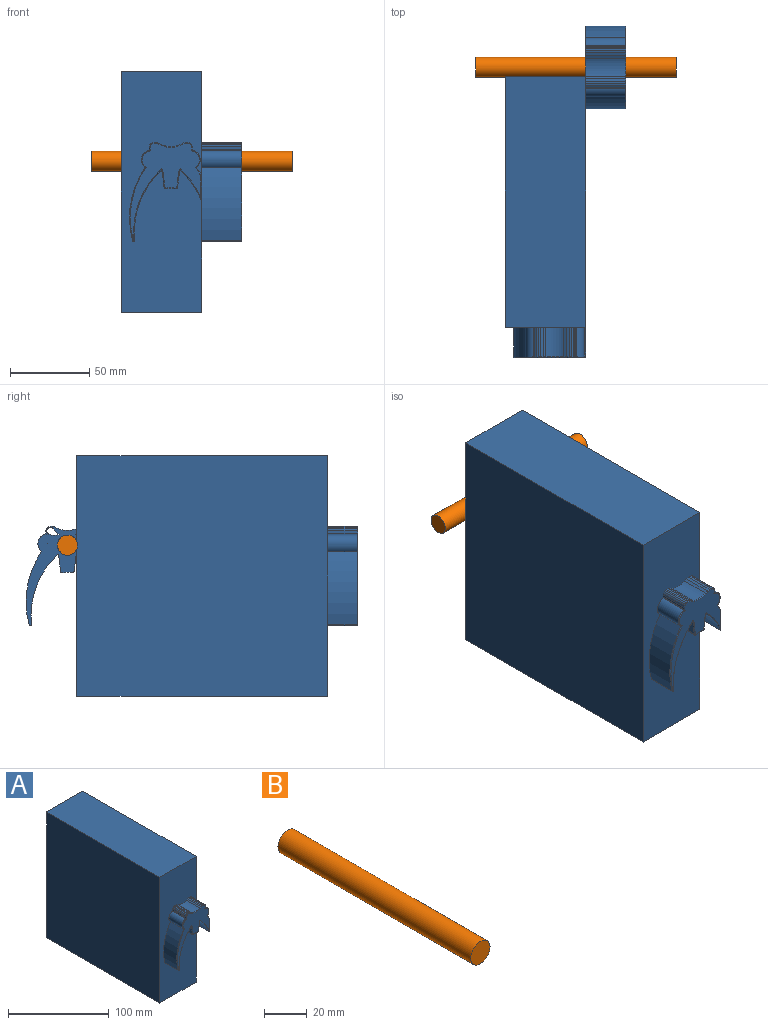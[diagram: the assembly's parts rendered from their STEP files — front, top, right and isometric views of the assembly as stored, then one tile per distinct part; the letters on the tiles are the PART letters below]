
ASSEMBLY  parts=2 mates=1
PART A: 129 faces, bbox 76.2x209.9x152.4 mm
  f0: plane 4.51x0.41mm, normal (1,0,0), area 1.3mm2, adj f6,f123
  f1: plane 7.02x5.02mm, normal (1,0,0), area 23.2mm2, adj f6,f82,f83,f122
  f2: plane 158.75x152.4mm, normal (-1,0,0), area 24193.5mm2, adj f3,f5,f6,f7
  f3: plane 158.75x50.8mm, normal (0,0,-1), area 8064.5mm2, adj f2,f4,f6,f7
  f4: plane 177.29x152.4mm, normal (1,0,0), area 24066.4mm2, adj f3,f5,f6,f7,f40,f41,f79,f87
  f5: plane 158.75x50.8mm, normal (0,0,1), area 8064.5mm2, adj f2,f4,f6,f7
  f6: plane 152.4x50.8mm, normal (0,1,0), area 7741.9mm2, adj f0,f1,f2,f3,f4,f5,f128
  f7: plane 152.4x50.8mm, normal (0,-1,0), area 6728.2mm2, adj f2,f3,f4,f5,f8,f9,f10,f11
  f8: plane 18.54x0.74mm, normal (-0.98,0,-0.2), area 14mm2, adj f7,f9,f27,f50
  f9: plane 18.54x1.46mm, normal (-1,0,0), area 27.1mm2, adj f7,f8,f10,f48
  f10: plane 18.54x1.2mm, normal (-0.96,0,0.27), area 23.2mm2, adj f7,f9,f11,f46
  f11: plane 18.54x0.9mm, normal (-0.81,0,0.59), area 20.6mm2, adj f7,f10,f12,f44
  f12: plane 18.54x0.95mm, normal (-0.51,0,0.86), area 20.5mm2, adj f7,f11,f13,f45
  f13: plane 18.54x1.21mm, normal (-0.17,0,0.99), area 22.8mm2, adj f7,f12,f14,f47
  f14: plane 18.54x1.43mm, normal (0.11,0,0.99), area 26.7mm2, adj f7,f13,f15,f49
  f15: plane 18.54x1.59mm, normal (0.31,0,0.95), area 31mm2, adj f7,f14,f26,f51
  f16: plane 18.54x1.69mm, normal (-0.45,0,0.89), area 35.2mm2, adj f7,f17,f25,f57
  f17: plane 18.54x1.59mm, normal (-0.31,0,0.95), area 31mm2, adj f7,f16,f18,f59
  f18: plane 18.54x1.43mm, normal (-0.11,0,0.99), area 26.7mm2, adj f7,f17,f19,f61
  f19: plane 18.54x1.21mm, normal (0.17,0,0.99), area 22.8mm2, adj f7,f18,f20,f63
  f20: plane 18.54x0.95mm, normal (0.51,0,0.86), area 20.5mm2, adj f7,f19,f21,f65
  f21: plane 18.54x0.9mm, normal (0.81,0,0.59), area 20.6mm2, adj f7,f20,f22,f67
  f22: plane 18.54x1.2mm, normal (0.96,0,0.27), area 23.2mm2, adj f7,f21,f23,f69
  f23: plane 18.54x1.46mm, normal (1,0,0), area 27.1mm2, adj f7,f22,f24,f71
  f24: plane 18.54x0.74mm, normal (0.98,0,-0.2), area 14mm2, adj f7,f23,f42,f73
  f25: cylinder r=14.29mm len=18.54mm, axis (0,1,0), area 217.9mm2, adj f7,f16,f26,f55
  f26: plane 18.54x1.69mm, normal (0.45,0,0.89), area 35.2mm2, adj f7,f15,f25,f53
  f27: cylinder r=6.29mm len=18.54mm, axis (0,1,0), area 265mm2, adj f7,f8,f28,f52
  f28: cylinder r=56.15mm len=46.32mm, axis (0,1,0), area 898.7mm2, adj f7,f27,f29,f54
  f29: cylinder r=0.67mm len=18.54mm, axis (0,1,0), area 18.2mm2, adj f7,f28,f30,f56
  f30: cylinder r=0.64mm len=18.54mm, axis (0,1,0), area 20.2mm2, adj f7,f29,f31,f58
  f31: cylinder r=53.73mm len=44.61mm, axis (0,1,0), area 915.5mm2, adj f7,f30,f32,f60
  f32: cylinder r=3.17mm len=18.54mm, axis (0,1,0), area 29.3mm2, adj f7,f31,f33,f62
  f33: plane 18.54x9.47mm, normal (-0.99,0,-0.12), area 176.9mm2, adj f7,f32,f34,f64
  f34: cylinder r=1.11mm len=18.54mm, axis (0,1,0), area 36.1mm2, adj f7,f33,f35,f66
  f35: cylinder r=10.43mm len=18.54mm, axis (0,1,0), area 53.3mm2, adj f7,f34,f36,f68
  f36: cylinder r=10.43mm len=18.54mm, axis (0,1,0), area 53.3mm2, adj f7,f35,f37,f70
  f37: cylinder r=1.11mm len=18.54mm, axis (0,1,0), area 36.1mm2, adj f7,f36,f38,f72
  f38: plane 18.54x9.47mm, normal (0.99,0,-0.12), area 176.9mm2, adj f7,f37,f39,f74
  f39: cylinder r=3.17mm len=18.54mm, axis (0,1,0), area 29.3mm2, adj f7,f38,f40,f76
  f40: cylinder r=53.72mm len=19.87mm, axis (0,1,0), area 448.4mm2, adj f4,f7,f39,f78
  f41: cylinder r=56.14mm len=18.54mm, axis (0,1,0), area 108.7mm2, adj f4,f7,f42,f77
  f42: cylinder r=6.29mm len=18.54mm, axis (0,1,0), area 265mm2, adj f7,f24,f41,f75
  f43: plane 61.88x44.54mm, normal (0,-1,0), area 892mm2, adj f44,f45,f46,f47,f48,f49,f50,f51
  f44: cylinder r=0.51mm len=1.2mm, axis (0.59,0,0.81), area 0.8mm2, adj f11,f43,f45,f46
  f45: cylinder r=0.51mm len=1.21mm, axis (0.86,0,0.51), area 0.8mm2, adj f12,f43,f44,f47
  f46: cylinder r=0.51mm len=1.34mm, axis (0.27,0,0.96), area 0.9mm2, adj f10,f43,f44,f48
  f47: cylinder r=0.51mm len=1.3mm, axis (0.99,0,0.17), area 0.9mm2, adj f13,f43,f45,f49
  f48: cylinder r=0.51mm len=1.46mm, axis (0,0,1), area 1.1mm2, adj f9,f43,f46,f50
  f49: cylinder r=0.51mm len=1.49mm, axis (0.99,0,-0.11), area 1.1mm2, adj f14,f43,f47,f51
  f50: cylinder r=0.51mm len=1.37mm, axis (-0.2,0,0.98), area 0.7mm2, adj f8,f43,f48,f52
  f51: cylinder r=0.51mm len=1.75mm, axis (0.95,0,-0.31), area 1.3mm2, adj f15,f43,f49,f53
  f52: torus R=5.78mm, axis (0,-1,0), area 11.4mm2, adj f27,f43,f50,f54
  f53: cylinder r=0.51mm len=1.94mm, axis (0.89,0,-0.45), area 1.5mm2, adj f26,f43,f51,f55
  f54: torus R=55.64mm, axis (0,-1,0), area 38.7mm2, adj f28,f43,f52,f56
  f55: torus R=14.8mm, axis (0,-1,0), area 9.5mm2, adj f25,f43,f53,f57
  f56: torus R=0.17mm, axis (0,-1,0), area 0.6mm2, adj f29,f43,f54,f58
  f57: cylinder r=0.51mm len=1.94mm, axis (0.89,0,0.45), area 1.5mm2, adj f16,f43,f55,f59
  f58: torus R=0.13mm, axis (0,-1,0), area 0.6mm2, adj f30,f43,f56,f60
  f59: cylinder r=0.51mm len=1.75mm, axis (0.95,0,0.31), area 1.3mm2, adj f17,f43,f57,f61
  f60: torus R=54.23mm, axis (0,-1,0), area 39.7mm2, adj f31,f43,f58,f62
  f61: cylinder r=0.51mm len=1.49mm, axis (0.99,0,0.11), area 1.1mm2, adj f18,f43,f59,f63
  f62: torus R=3.68mm, axis (0,-1,0), area 1.5mm2, adj f32,f43,f60,f64
  f63: cylinder r=0.51mm len=1.3mm, axis (0.99,0,-0.17), area 0.9mm2, adj f19,f43,f61,f65
  f64: cylinder r=0.51mm len=9.53mm, axis (-0.12,0,0.99), area 7.6mm2, adj f33,f43,f62,f66
  f65: cylinder r=0.51mm len=1.21mm, axis (0.86,0,-0.51), area 0.8mm2, adj f20,f43,f63,f67
  f66: torus R=0.6mm, axis (0,-1,0), area 1.3mm2, adj f34,f43,f64,f68
  f67: cylinder r=0.51mm len=1.2mm, axis (0.59,0,-0.81), area 0.8mm2, adj f21,f43,f65,f69
  f68: torus R=10.94mm, axis (0,-1,0), area 2.3mm2, adj f35,f43,f66,f70
  f69: cylinder r=0.51mm len=1.34mm, axis (0.27,0,-0.96), area 0.9mm2, adj f22,f43,f67,f71
  f70: torus R=10.94mm, axis (0,-1,0), area 2.3mm2, adj f36,f43,f68,f72
  f71: cylinder r=0.51mm len=1.46mm, axis (0,0,-1), area 1.1mm2, adj f23,f43,f69,f73
  f72: torus R=0.6mm, axis (0,-1,0), area 1.3mm2, adj f37,f43,f70,f74
  f73: cylinder r=0.51mm len=1.37mm, axis (-0.2,0,-0.98), area 0.7mm2, adj f24,f43,f71,f75
  f74: cylinder r=0.51mm len=9.53mm, axis (-0.12,0,-0.99), area 7.6mm2, adj f38,f43,f72,f76
  f75: torus R=5.78mm, axis (0,-1,0), area 11.4mm2, adj f42,f43,f73,f77
  f76: torus R=3.68mm, axis (0,-1,0), area 1.5mm2, adj f39,f43,f74,f78
  f77: torus R=55.64mm, axis (0,-1,0), area 4.7mm2, adj f41,f43,f75,f79
  f78: torus R=54.23mm, axis (0,-1,0), area 18.8mm2, adj f40,f43,f76,f79
  f79: cylinder r=0.51mm len=16.36mm, axis (0,0,-1), area 12.2mm2, adj f4,f43,f77,f78
  f80: cylinder r=8.13mm len=25.4mm, axis (-1,0,0), area 168.6mm2, adj f81,f126,f127,f128
  f81: cylinder r=10.32mm len=25.4mm, axis (-1,0,0), area 132.3mm2, adj f80,f126,f127,f128
  f82: cylinder r=10.32mm len=25.4mm, axis (-1,0,0), area 132.3mm2, adj f1,f83,f122,f127,f128
  f83: cylinder r=8.13mm len=25.4mm, axis (-1,0,0), area 168.6mm2, adj f1,f82,f122,f127,f128
  f84: plane 25.4x0mm, normal (0,-0.73,0.68), area 0mm2, adj f85,f124,f127,f128
  f85: cylinder r=56.14mm len=25.4mm, axis (-1,0,0), area 0mm2, adj f84,f124,f127,f128
  f86: cylinder r=14.29mm len=25.4mm, axis (-1,0,0), area 298.5mm2, adj f87,f125,f127,f128
  f87: plane 25.4x1.69mm, normal (0,0.45,0.89), area 48.3mm2, adj f4,f86,f88,f127,f128
  f88: plane 25.4x1.59mm, normal (0,0.31,0.95), area 42.5mm2, adj f4,f87,f89,f127
  f89: plane 25.4x1.43mm, normal (0,0.11,0.99), area 36.5mm2, adj f4,f88,f90,f127
  f90: plane 25.4x1.21mm, normal (0,-0.17,0.99), area 31.3mm2, adj f4,f89,f91,f127
  f91: plane 25.4x0.95mm, normal (0,-0.51,0.86), area 28.1mm2, adj f4,f90,f92,f127
  f92: plane 25.4x0.9mm, normal (0,-0.81,0.59), area 28.3mm2, adj f4,f91,f93,f127
  f93: plane 25.4x1.2mm, normal (0,-0.96,0.27), area 31.7mm2, adj f4,f92,f94,f127
  f94: plane 25.4x1.46mm, normal (0,-1,0), area 37.1mm2, adj f4,f93,f95,f127
  f95: plane 25.4x0.74mm, normal (0,-0.98,-0.2), area 19.2mm2, adj f4,f94,f96,f127
  f96: cylinder r=6.29mm len=25.4mm, axis (-1,0,0), area 363mm2, adj f4,f95,f97,f127
  f97: cylinder r=56.15mm len=46.32mm, axis (-1,0,0), area 1231.1mm2, adj f4,f96,f98,f127
  f98: cylinder r=0.67mm len=25.4mm, axis (-1,0,0), area 24.9mm2, adj f4,f97,f99,f127
  f99: cylinder r=0.64mm len=25.4mm, axis (-1,0,0), area 27.7mm2, adj f4,f98,f100,f127
  f100: cylinder r=53.73mm len=44.61mm, axis (-1,0,0), area 1254.2mm2, adj f4,f99,f101,f127
  f101: cylinder r=3.17mm len=25.4mm, axis (-1,0,0), area 40.2mm2, adj f4,f100,f102,f127,f128
  f102: plane 25.4x9.47mm, normal (0,-0.99,-0.12), area 242.3mm2, adj f101,f103,f127,f128
  f103: cylinder r=1.11mm len=25.4mm, axis (-1,0,0), area 49.4mm2, adj f102,f104,f127,f128
  f104: cylinder r=10.43mm len=25.4mm, axis (-1,0,0), area 73.1mm2, adj f103,f105,f127,f128
  f105: cylinder r=10.43mm len=25.4mm, axis (-1,0,0), area 73.1mm2, adj f104,f106,f127,f128
  f106: cylinder r=1.11mm len=25.4mm, axis (-1,0,0), area 49.4mm2, adj f105,f107,f127,f128
  f107: plane 25.4x9.47mm, normal (0,0.99,-0.12), area 242.3mm2, adj f106,f108,f127,f128
  f108: cylinder r=3.17mm len=25.4mm, axis (-1,0,0), area 40.2mm2, adj f107,f109,f127,f128
  f109: cylinder r=53.72mm len=44.61mm, axis (-1,0,0), area 1254.1mm2, adj f108,f110,f127,f128
  f110: cylinder r=0.64mm len=25.4mm, axis (-1,0,0), area 27.7mm2, adj f109,f111,f127,f128
  f111: cylinder r=0.67mm len=25.4mm, axis (-1,0,0), area 24.9mm2, adj f110,f112,f127,f128
  f112: cylinder r=56.14mm len=46.32mm, axis (-1,0,0), area 1231mm2, adj f111,f113,f127,f128
  f113: cylinder r=6.29mm len=25.4mm, axis (-1,0,0), area 363mm2, adj f112,f114,f127,f128
  f114: plane 25.4x0.74mm, normal (0,0.98,-0.2), area 19.2mm2, adj f113,f115,f127,f128
  f115: plane 25.4x1.46mm, normal (0,1,0), area 37.1mm2, adj f114,f116,f127,f128
  f116: plane 25.4x1.2mm, normal (0,0.96,0.27), area 31.7mm2, adj f115,f117,f127,f128
  f117: plane 25.4x0.9mm, normal (0,0.81,0.59), area 28.3mm2, adj f116,f118,f127,f128
  f118: plane 25.4x0.95mm, normal (0,0.51,0.86), area 28.1mm2, adj f117,f119,f127,f128
  f119: plane 25.4x1.21mm, normal (0,0.17,0.99), area 31.3mm2, adj f118,f120,f127,f128
  f120: plane 25.4x1.43mm, normal (0,-0.11,0.99), area 36.5mm2, adj f119,f121,f127,f128
  f121: plane 25.4x1.59mm, normal (0,-0.31,0.95), area 42.5mm2, adj f120,f125,f127,f128
  f122: cylinder r=2.26mm len=25.4mm, axis (-1,0,0), area 208.3mm2, adj f1,f82,f83,f127
  f123: cylinder r=6.35mm len=25.4mm, axis (-1,0,0), area 1013.4mm2, adj f0,f127,f128
  f124: cylinder r=20.39mm len=25.4mm, axis (-1,0,0), area 0mm2, adj f84,f85,f127,f128
  f125: plane 25.4x1.69mm, normal (0,-0.45,0.89), area 48.3mm2, adj f86,f121,f127,f128
  f126: cylinder r=2.26mm len=25.4mm, axis (-1,0,0), area 208.3mm2, adj f80,f81,f127,f128
  f127: plane 62.9x52.28mm, normal (1,0,0), area 984mm2, adj f80,f81,f82,f83,f84,f85,f86,f87
  f128: plane 62.9x32.12mm, normal (-1,0,0), area 578mm2, adj f6,f80,f81,f82,f83,f84,f85,f86
PART B: 3 faces, bbox 12.7x127x12.7 mm
  f0: cylinder r=6.35mm len=127mm, axis (0,1,0), area 5067.1mm2, adj f1,f2
  f1: plane 12.7x12.7mm, normal (0,-1,0), area 126.7mm2, adj f0
  f2: plane 12.7x12.7mm, normal (0,1,0), area 126.7mm2, adj f0
PLACE A t=(-12.73,72.72,-0.19)mm fixed
PLACE B rot(axis=(0.58,-0.58,0.58),120deg) t=(-56.86,78.66,19.29)mm
MATE slider B.f0 <-> A.f123  axis (-1,0,0) through (6.64,78.66,19.29)mm
